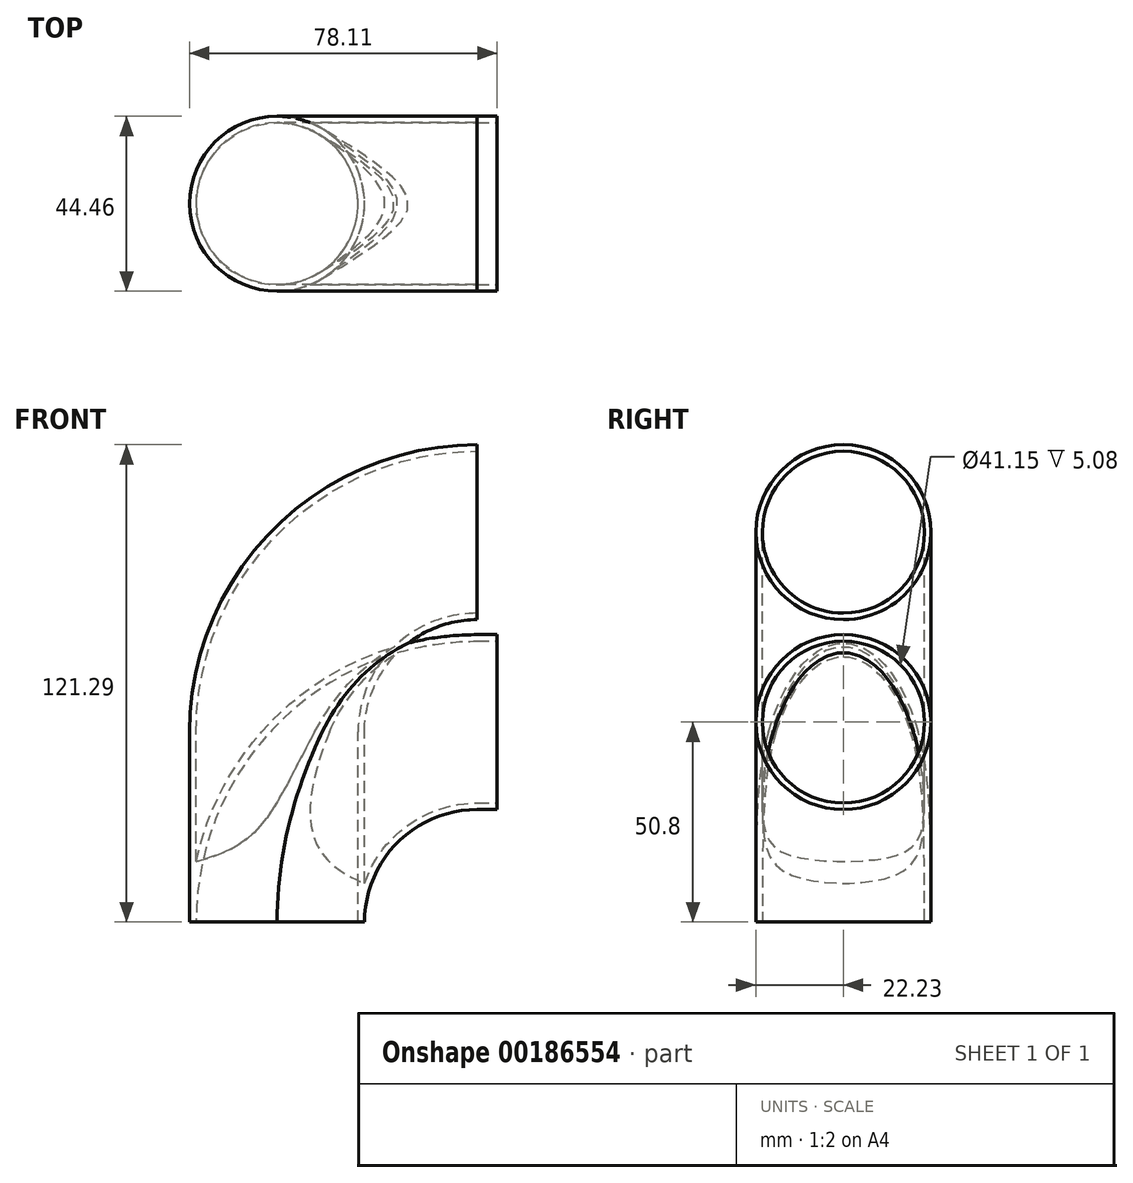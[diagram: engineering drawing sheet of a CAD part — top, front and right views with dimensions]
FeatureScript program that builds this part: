
annotation { "Feature Type Name" : "Feature", "Feature Type Description" : "" }
export const myFeature = defineFeature(function(context is Context, id is Id, definition is map)
    precondition{}
    {
        {
            var Q0;
            Q0=qCreatedBy(makeId("Front.planeOp"),FACE);
            var sketch = newSketch(context, id + "F0", { "sketchPlane" : qUnion([Q0])});
            skArc(sketch, "E0.filletArc", {"start": v(50.8, 50.8) * mm, "mid": v(14.88, 35.92) * mm, "end": v(0, 0) * mm});
            skLineSegment(sketch, "E1", {"start": v(0, 0) * mm, "end": v(0, 48.26) * mm});
            skArc(sketch, "E2.filletArc", {"start": v(50.8, 99.06) * mm, "mid": v(14.88, 84.18) * mm, "end": v(0, 48.26) * mm});
            skLineSegment(sketch, "E3", {"start": v(50.8, 50.8) * mm, "end": v(55.88, 50.8) * mm});
            skSolve(sketch);
        }
        {
            var Q0;
            Q0=qCreatedBy(makeId("Top.planeOp"),FACE);
            var sketch = newSketch(context, id + "F1", { "sketchPlane" : qUnion([Q0])});
            skCircle(sketch, "E4", {"center": v(0, 0) * mm, "radius": 20.57 * mm});
            skCircle(sketch, "E5", {"center": v(0, 0) * mm, "radius": 22.23 * mm});
            skSolve(sketch);
        }
        {
            var Q0;
            Q0 = qSketchRegion(id + "F1", true);
            var Q1;
            Q1=sQuery(id+"F0.wireOp",EDGE,"E0.filletArc");
            var Q2;
            Q2=sQuery(id+"F0.wireOp",EDGE,"E3");
            sweep(context, id + "F2", {"profiles" : qUnion([Q0]), "path" : qUnion([Q1, Q2])});
        }
        {
            var Q0;
            Q0 = qSketchRegion(id + "F1", true);
            var Q1;
            Q1=sQuery(id+"F0.wireOp",EDGE,"E1");
            var Q2;
            Q2=sQuery(id+"F0.wireOp",EDGE,"E2.filletArc");
            sweep(context, id + "F3", {"operationType" : NewBodyOperationType.ADD, "profiles" : qUnion([Q0]), "path" : qUnion([Q1, Q2])});
        }
    });
